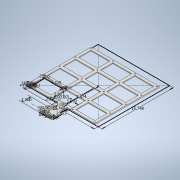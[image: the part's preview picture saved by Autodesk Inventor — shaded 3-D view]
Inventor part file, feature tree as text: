
AUTODESK INVENTOR PART (.ipt)
format: ipt  version: 2020 (Build 240168000, 168)  size: 302,080 bytes
history: native  units: in
note: dims shown in document units (in); Inventor stores cm internally (conversion verified against a paired STEP export)
features: extrude x4, sketch x3, hole x2, pattern_linear x1
ambient origin geometry x8: Origin, YZ Plane, XZ Plane, XY Plane, X Axis, Y Axis, Z Axis, Center Point
bodies: Solid1 (feature_tree)
feature tree (10):
  sketch  "Sketch1"  dims[d0=3.0in d1=2.0in]
  extrude  "Extrusion1"  Depth=2.0in
  hole  "Hole1"  [1 undecoded]
  sketch  "Sketch2"  dims[d2=0.25in d3=1.0in]
  extrude  "Extrusion2"  TaperAngle=0.0deg  [1 undecoded]
  hole  "Hole2"  [1 undecoded]
  extrude  "Extrusion3"  Depth=0.5in
  pattern_linear  "Rectangular Pattern1"  Spacing1=0.25in  [1 undecoded]
  extrude  "Extrusion4"  Depth=0.25in
  sketch  "Sketch3"  dims[d4=1.0in d5=0.0in d6=0.5in d7=0.5in d8=0.25in d9=0.25in d10=2.9528in d11=90.0deg d12=2.9528in d13=1.0in d14=7.874in d15=90.0deg d16=15.748in d17=15.748in d18=0.25in d19=0.0in d20=0.26in d21=0.5in d22=0.375in d23=0.25in d24=0.5635in d25=1.0in d26=0.8108in d27=0.25in d28=90.0deg d29=0.25in d30=0.25in d31=0.25in d32=4.3386in d33=2.9134in d34=0.25in d35=0.25in d36=0.25in d37=0.25in d38=0.25in d39=0.315in d40=90.0deg d41=0.0787in d42=0.0787in d43=0.0787in d44=0.0787in d45=0.0in d46=0.0in d47=0.203in d48=0.625in d49=0.375in d50=0.25in d51=0.5635in d52=1.0in d53=0.8108in d54=0.0787in d55=0.0in d56=1.1811in d58=4.839in d59=1.5748in d61=3.423in d62=0.25in d63=0.25in d64=0.0in d65=0.0in]
note: 4 required parameter values undecoded (feature->parameter linkage not recoverable at this tier; creation-order binding heuristic only, values carry confidence <= 0.55)
